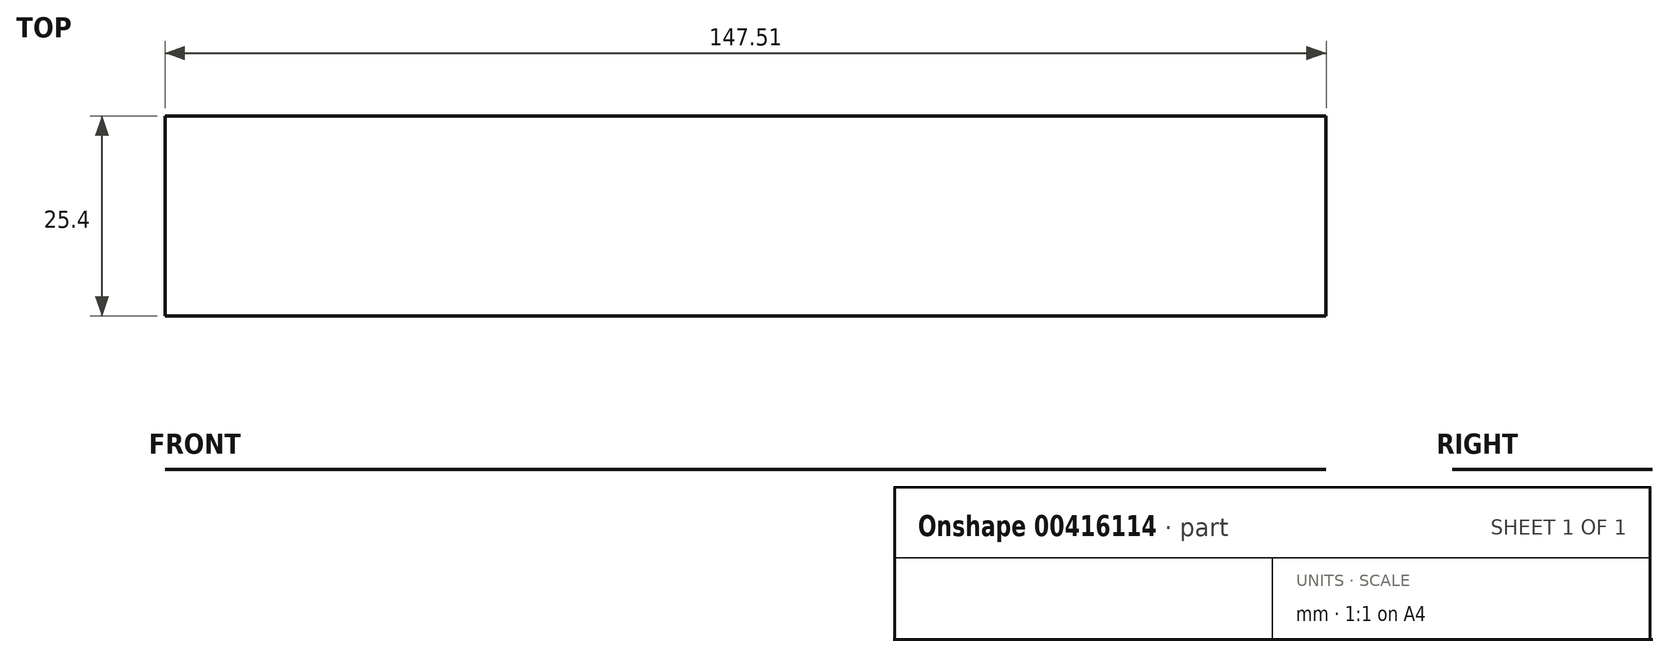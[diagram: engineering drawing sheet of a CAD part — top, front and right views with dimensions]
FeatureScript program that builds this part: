
annotation { "Feature Type Name" : "Feature", "Feature Type Description" : "" }
export const myFeature = defineFeature(function(context is Context, id is Id, definition is map)
    precondition{}
    {
        {
            var Q0;
            Q0=qCreatedBy(makeId("Front.planeOp"),FACE);
            var sketch = newSketch(context, id + "F0", { "sketchPlane" : qUnion([Q0])});
            skLineSegment(sketch, "E0.bottom", {"start": v(39.95, -16.3) * mm, "end": v(46.42, -16.3) * mm});
            skLineSegment(sketch, "E0.top", {"start": v(39.95, -39.74) * mm, "end": v(46.42, -39.74) * mm});
            skLineSegment(sketch, "E0.left", {"start": v(39.95, -16.3) * mm, "end": v(39.95, -39.74) * mm});
            skLineSegment(sketch, "E0.right", {"start": v(46.42, -16.3) * mm, "end": v(46.42, -39.74) * mm});
            skLineSegment(sketch, "E1.bottom", {"start": v(-27, 0) * mm, "end": v(120.5, 0) * mm});
            skLineSegment(sketch, "E1.top", {"start": v(-27, 125.84) * mm, "end": v(120.5, 125.84) * mm});
            skLineSegment(sketch, "E1.left", {"start": v(-27, 0) * mm, "end": v(-27, 125.84) * mm});
            skLineSegment(sketch, "E1.right", {"start": v(120.5, 0) * mm, "end": v(120.5, 125.84) * mm});
            skSolve(sketch);
        }
        {
            var Q0;
            Q0=sQuery(id+"F0.wireOp",EDGE,"E1.top");
            extrude(context, id + "F1", {"bodyType" : ToolBodyType.SURFACE, "surfaceEntities" : qUnion([Q0]), "oppositeDirection" : true, "depth" : 25.4 * mm});
        }
    });
